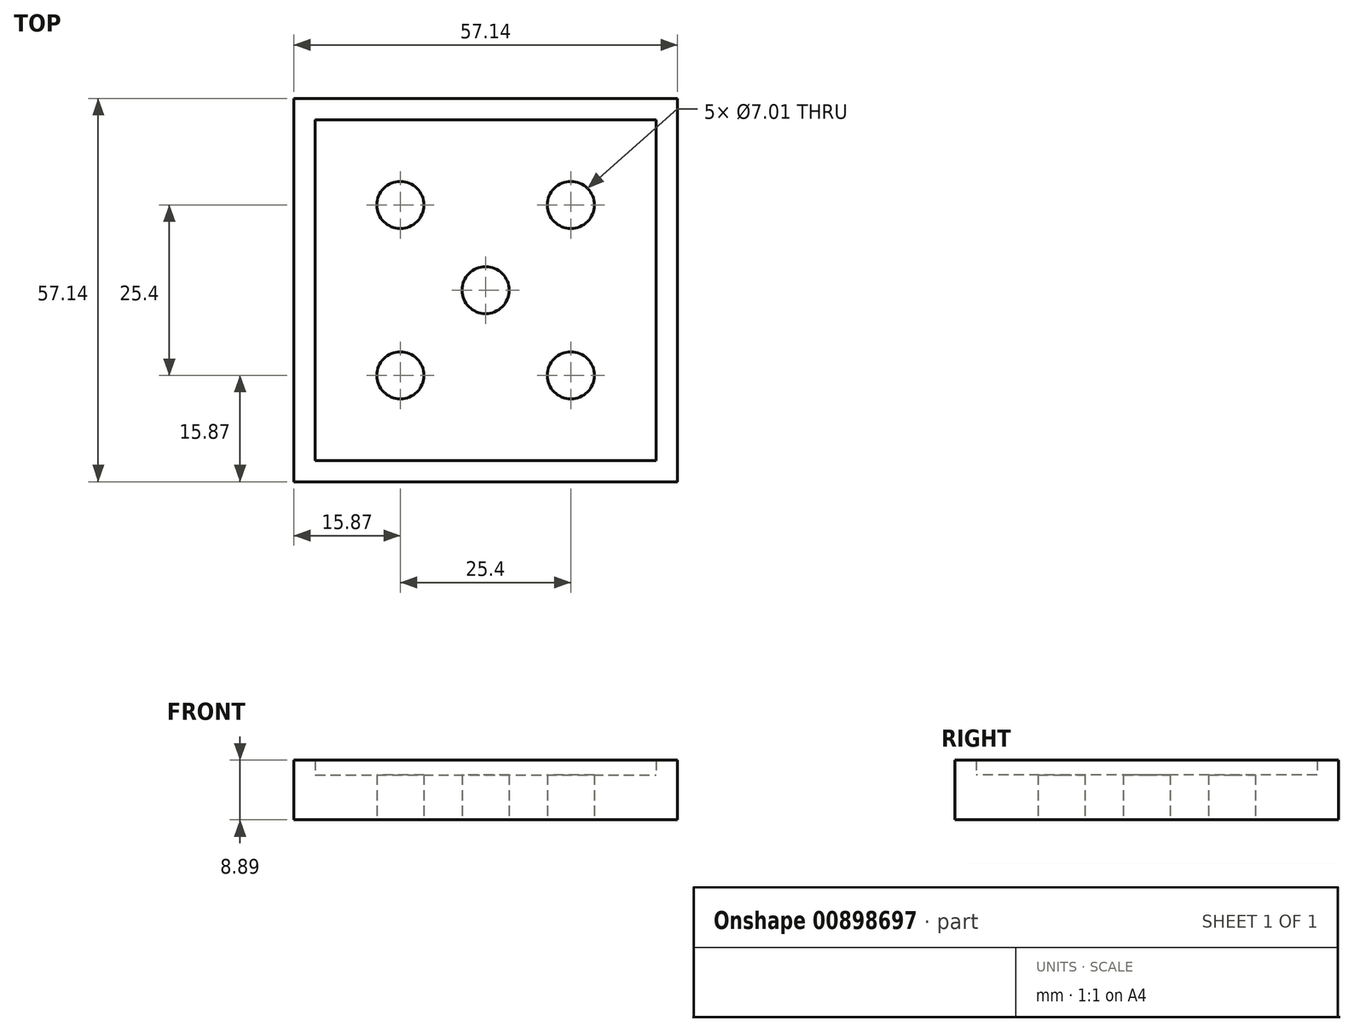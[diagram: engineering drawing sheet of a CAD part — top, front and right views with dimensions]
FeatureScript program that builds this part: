
annotation { "Feature Type Name" : "Feature", "Feature Type Description" : "" }
export const myFeature = defineFeature(function(context is Context, id is Id, definition is map)
    precondition{}
    {
        {
            var Q0;
            Q0=qCreatedBy(makeId("Top.planeOp"),FACE);
            var sketch = newSketch(context, id + "F0", { "sketchPlane" : qUnion([Q0])});
            skLineSegment(sketch, "E0.bottom", {"start": v(-28.58, 28.58) * mm, "end": v(28.58, 28.58) * mm});
            skLineSegment(sketch, "E0.top", {"start": v(-28.58, -28.58) * mm, "end": v(28.58, -28.58) * mm});
            skLineSegment(sketch, "E0.left", {"start": v(-28.58, 28.58) * mm, "end": v(-28.58, -28.58) * mm});
            skLineSegment(sketch, "E0.right", {"start": v(28.57, 28.58) * mm, "end": v(28.58, -28.57) * mm});
            skLineSegment(sketch, "E1", {"start": v(-28.58, 0) * mm, "end": v(28.58, 0) * mm, "construction": true});
            skLineSegment(sketch, "E2", {"start": v(0, 28.58) * mm, "end": v(0, -28.58) * mm, "construction": true});
            skLineSegment(sketch, "E3.0", {"start": v(-25.4, 25.4) * mm, "end": v(-25.4, -25.4) * mm});
            skLineSegment(sketch, "E3.1", {"start": v(-25.4, 25.4) * mm, "end": v(25.4, 25.4) * mm});
            skLineSegment(sketch, "E3.2", {"start": v(25.4, 25.4) * mm, "end": v(25.4, -25.4) * mm});
            skLineSegment(sketch, "E3.3", {"start": v(-25.4, -25.4) * mm, "end": v(25.4, -25.4) * mm});
            skCircle(sketch, "E4", {"center": v(0, 0) * mm, "radius": 3.5 * mm});
            skCircle(sketch, "E5", {"center": v(-12.7, -12.7) * mm, "radius": 3.5 * mm});
            skCircle(sketch, "E6.0.1.0", {"center": v(-12.7, 12.7) * mm, "radius": 3.5 * mm});
            skCircle(sketch, "E6.1.0.0", {"center": v(12.7, -12.7) * mm, "radius": 3.5 * mm});
            skCircle(sketch, "E6.1.1.0", {"center": v(12.7, 12.7) * mm, "radius": 3.5 * mm});
            skLineSegment(sketch, "E6.direction1", {"start": v(-12.7, -12.7) * mm, "end": v(12.7, -12.7) * mm, "construction": true});
            skLineSegment(sketch, "E6.direction2", {"start": v(-12.7, -12.7) * mm, "end": v(-12.7, 12.7) * mm, "construction": true});
            skSolve(sketch);
        }
        {
            var Q0;
            Q0=makeQuery(id+"F0.imprint","IMPRINT",FACE,{"disambiguationData":[TD([[makeQuery(id+"F0.imprint","IMPRINT",EDGE,{"derivedFrom":sQuery(id+"F0.wireOp",EDGE,"E3.0")}),1.0]])]});
            extrude(context, id + "F1", {"entities" : qUnion([Q0]), "depth" : 6.7 * mm, "offsetDistance" : 25.4 * mm});
        }
        {
            var Q0;
            Q0=makeQuery(id+"F0.imprint","IMPRINT",FACE,{"disambiguationData":[TD([[makeQuery(id+"F0.imprint","IMPRINT",EDGE,{"derivedFrom":sQuery(id+"F0.wireOp",EDGE,"E0.bottom")}),-1.0]])]});
            extrude(context, id + "F2", {"entities" : qUnion([Q0]), "operationType" : NewBodyOperationType.ADD, "depth" : 8.9 * mm, "offsetDistance" : 25.4 * mm});
        }
    });
